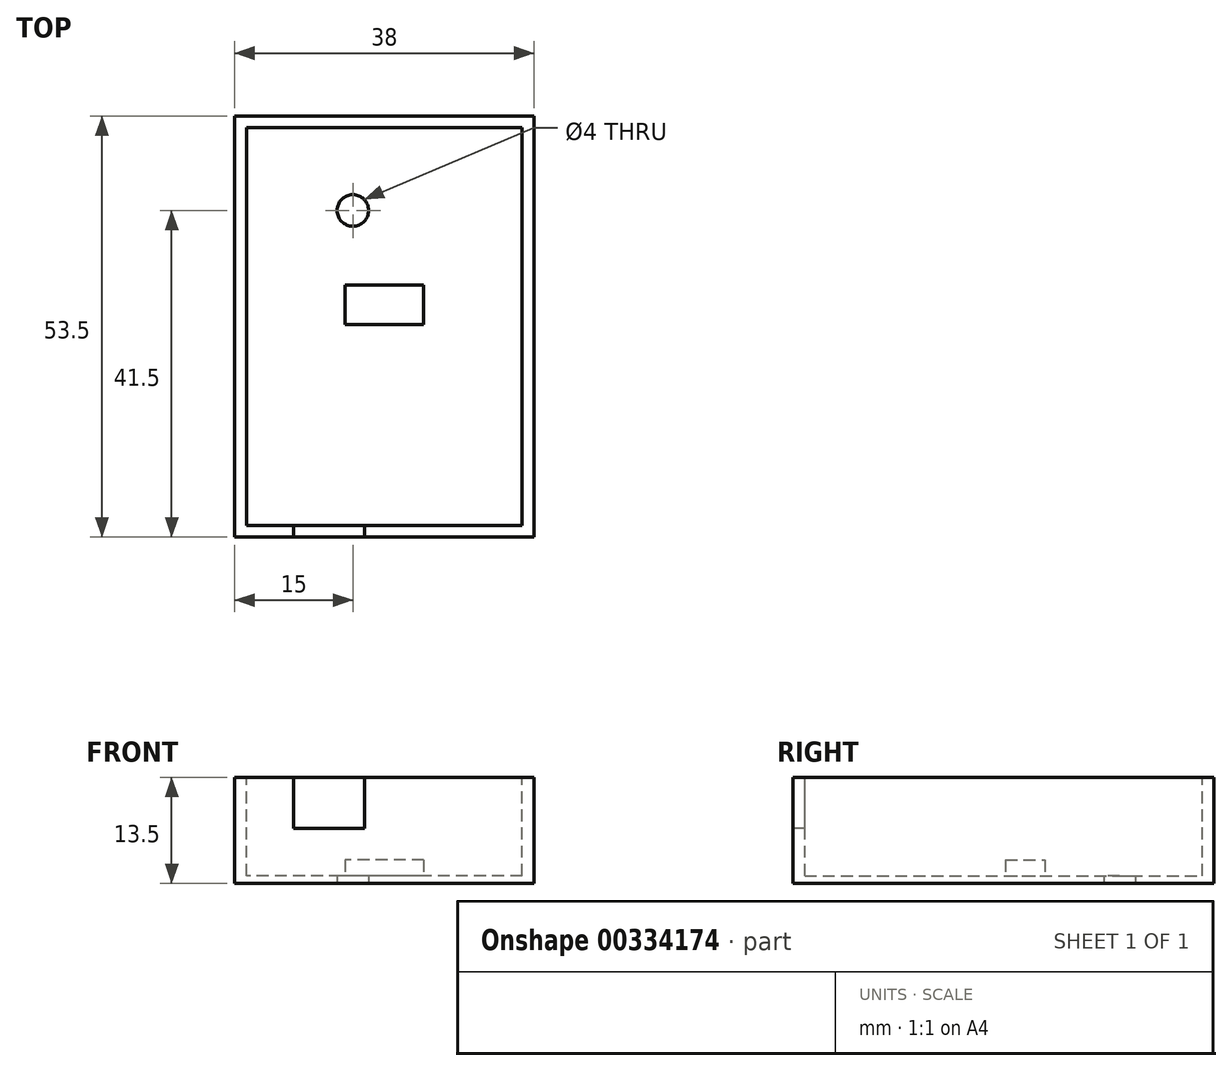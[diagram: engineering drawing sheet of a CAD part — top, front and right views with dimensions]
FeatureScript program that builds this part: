
annotation { "Feature Type Name" : "Feature", "Feature Type Description" : "" }
export const myFeature = defineFeature(function(context is Context, id is Id, definition is map)
    precondition{}
    {
        {
            var Q0;
            Q0=qCreatedBy(makeId("Top.planeOp"),FACE);
            var sketch = newSketch(context, id + "F0", { "sketchPlane" : qUnion([Q0])});
            skLineSegment(sketch, "E0.bottom", {"start": v(19, -26.75) * mm, "end": v(-19, -26.75) * mm});
            skLineSegment(sketch, "E0.top", {"start": v(19, 26.75) * mm, "end": v(-19, 26.75) * mm});
            skLineSegment(sketch, "E0.left", {"start": v(19, -26.75) * mm, "end": v(19, 26.75) * mm});
            skLineSegment(sketch, "E0.right", {"start": v(-19, -26.75) * mm, "end": v(-19, 26.75) * mm});
            skPoint(sketch, "E0.middle", {"position": v(0, 0) * mm});
            skSolve(sketch);
        }
        {
            var Q0;
            Q0 = qSketchRegion(id + "F0", true);
            extrude(context, id + "F1", {"entities" : qUnion([Q0]), "depth" : 13.5 * mm});
        }
        {
            var Q0;
            Q0=makeQuery(id+"F1.opExtrude","CAP_FACE",FACE,{"disambiguationData":[OSD([sQuery(id+"F0.wireOp",EDGE,"E0.bottom"),sQuery(id+"F0.wireOp",EDGE,"E0.top"),sQuery(id+"F0.wireOp",EDGE,"E0.left"),sQuery(id+"F0.wireOp",EDGE,"E0.right")])],"isStart":false});
            var sketch = newSketch(context, id + "F2", { "sketchPlane" : qUnion([Q0])});
            skLineSegment(sketch, "E1.bottom", {"start": v(17.5, -25.25) * mm, "end": v(-17.5, -25.25) * mm});
            skLineSegment(sketch, "E1.top", {"start": v(17.5, 25.25) * mm, "end": v(-17.5, 25.25) * mm});
            skLineSegment(sketch, "E1.left", {"start": v(17.5, -25.25) * mm, "end": v(17.5, 25.25) * mm});
            skLineSegment(sketch, "E1.right", {"start": v(-17.5, -25.25) * mm, "end": v(-17.5, 25.25) * mm});
            skPoint(sketch, "E1.middle", {"position": v(0, 0) * mm});
            skSolve(sketch);
        }
        {
            var Q0;
            Q0 = qSketchRegion(id + "F2", true);
            extrude(context, id + "F3", {"entities" : qUnion([Q0]), "operationType" : NewBodyOperationType.REMOVE, "oppositeDirection" : true, "depth" : 12.5 * mm});
        }
        {
            var Q0;
            Q0=makeQuery(id+"F1.opExtrude","CAP_FACE",FACE,{"disambiguationData":[OSD([sQuery(id+"F0.wireOp",EDGE,"E0.bottom"),sQuery(id+"F0.wireOp",EDGE,"E0.top"),sQuery(id+"F0.wireOp",EDGE,"E0.left"),sQuery(id+"F0.wireOp",EDGE,"E0.right")])],"isStart":true});
            var sketch = newSketch(context, id + "F4", { "sketchPlane" : qUnion([Q0])});
            skCircle(sketch, "E2", {"center": v(-4, -14.75) * mm, "radius": 2 * mm});
            skSolve(sketch);
        }
        {
            var Q0;
            Q0 = qSketchRegion(id + "F4", true);
            extrude(context, id + "F5", {"entities" : qUnion([Q0]), "operationType" : NewBodyOperationType.REMOVE, "oppositeDirection" : true, "depth" : 25 * mm});
        }
        {
            var Q0;
            Q0=makeQuery(id+"F1.opExtrude","SWEPT_FACE",FACE,{"disambiguationData":[OSD([sQuery(id+"F0.wireOp",EDGE,"E0.bottom")])]});
            var sketch = newSketch(context, id + "F6", { "sketchPlane" : qUnion([Q0])});
            skLineSegment(sketch, "E3.bottom", {"start": v(-11.5, 13.5) * mm, "end": v(-2.5, 13.5) * mm});
            skLineSegment(sketch, "E3.top", {"start": v(-11.5, 7) * mm, "end": v(-2.5, 7) * mm});
            skLineSegment(sketch, "E3.left", {"start": v(-11.5, 13.5) * mm, "end": v(-11.5, 7) * mm});
            skLineSegment(sketch, "E3.right", {"start": v(-2.5, 13.5) * mm, "end": v(-2.5, 7) * mm});
            skSolve(sketch);
        }
        {
            var Q0;
            Q0 = qSketchRegion(id + "F6", true);
            extrude(context, id + "F7", {"entities" : qUnion([Q0]), "operationType" : NewBodyOperationType.REMOVE, "oppositeDirection" : true, "depth" : 25 * mm});
        }
        {
            var Q0;
            Q0=makeQuery(id+"F7.boolean.opBoolean","MERGE",FACE,{"derivedFrom":[makeQuery(id+"F3.boolean.opBoolean","COPY",FACE,{"derivedFrom":makeQuery(id+"F3.opExtrude","CAP_FACE",FACE,{"disambiguationData":[OSD([sQuery(id+"F2.wireOp",EDGE,"E1.bottom"),sQuery(id+"F2.wireOp",EDGE,"E1.top"),sQuery(id+"F2.wireOp",EDGE,"E1.left"),sQuery(id+"F2.wireOp",EDGE,"E1.right")])],"isStart":false})}),makeQuery(id+"F7.opExtrude","SWEPT_FACE",FACE,{"disambiguationData":[OSD([sQuery(id+"F6.wireOp",EDGE,"E3.top")])]})]});
            var sketch = newSketch(context, id + "F8", { "sketchPlane" : qUnion([Q0])});
            skLineSegment(sketch, "E4.bottom", {"start": v(5, 0.25) * mm, "end": v(-5, 0.25) * mm});
            skLineSegment(sketch, "E4.top", {"start": v(5, 5.25) * mm, "end": v(-5, 5.25) * mm});
            skLineSegment(sketch, "E4.left", {"start": v(5, 0.25) * mm, "end": v(5, 5.25) * mm});
            skLineSegment(sketch, "E4.right", {"start": v(-5, 0.25) * mm, "end": v(-5, 5.25) * mm});
            skPoint(sketch, "E4.middle", {"position": v(0, 2.75) * mm});
            skSolve(sketch);
        }
        {
            var Q0;
            Q0 = qSketchRegion(id + "F8", true);
            extrude(context, id + "F9", {"entities" : qUnion([Q0]), "operationType" : NewBodyOperationType.ADD, "depth" : 2 * mm});
        }
    });
